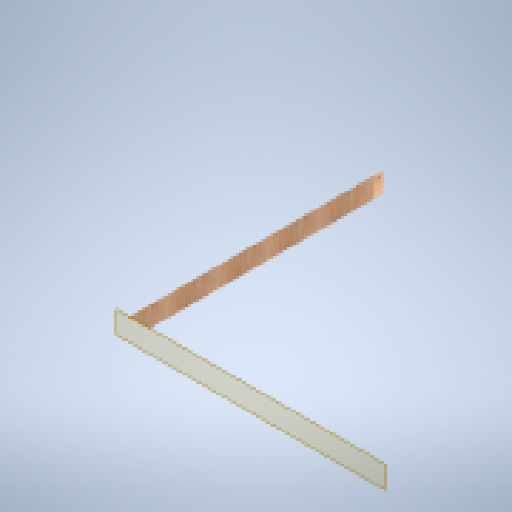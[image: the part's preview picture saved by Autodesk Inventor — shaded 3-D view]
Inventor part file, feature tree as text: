
AUTODESK INVENTOR PART (.ipt)
format: ipt  version: 2025 (Build 290162000, 162)  size: 142,848 bytes
history: native  units: in
note: dims shown in document units (in); Inventor stores cm internally (conversion verified against a paired STEP export)
features: other x4, reference x2, plane x1, extrude x1, sketch x1
ambient origin geometry x8: Origin, YZ Plane, XZ Plane, XY Plane, X Axis, Y Axis, Z Axis, Center Point
bodies: Solid1 (feature_tree)
feature tree (9):
  plane  "Work Plane1"
  extrude  "Extrusion1"  Depth=2.0in
  sketch  "Sketch1"  dims[d0=4.0in d1=4.0in d2=2.0in d3=0.0in]
  reference  "Reference1"
  reference  "Reference2"
  other  "<userpath>\Documents\GitHub\USCTigerBurn24\v2\Tiger.iam"
  other  "Tiger.iam"
  other  "2x4x48:14"
  other  "2x4x48:10"
